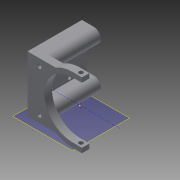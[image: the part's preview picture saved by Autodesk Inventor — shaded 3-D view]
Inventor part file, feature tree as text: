
AUTODESK INVENTOR PART (.ipt)
format: ipt  version: 2015 SP2 (Build 190223200, 223)  size: 181,248 bytes
history: native  units: mm
features: sketch x8, extrude x4, hole x3, plane x1
ambient origin geometry x8: Origin, YZ Plane, XZ Plane, XY Plane, X Axis, Y Axis, Z Axis, Center Point
bodies: Solid1 (feature_tree)
feature tree (16):
  extrude  "Extrusion1"  Depth=50.0mm TaperAngle=0.0deg
  extrude  "Extrusion2"  Depth=10.0mm
  extrude  "Extrusion3"  Depth=15.0mm
  hole  "Hole1"  [1 undecoded]
  plane  "Work Plane1"
  hole  "Hole2"  [1 undecoded]
  sketch  "Sketch7"  dims[d36=4.5mm d37=6.0mm d38=10.59mm d39=3.0mm d40=90.0deg d41=8.0mm d42=20.594885mm d44=4.0mm d45=0.0mm]
  hole  "Hole3"  [1 undecoded]
  extrude  "Extrusion4"  [1 undecoded]
  sketch  "Sketch1"  dims[d5=0.0mm d7=50.0mm d8=0.0mm]
  sketch  "Sketch2"  dims[d12=50.0mm d13=0.0mm]
  sketch  "Sketch3"  dims[d17=3.4mm d18=6.0mm d19=4.0mm d20=2.0mm d21=90.0deg d22=8.0mm d23=20.594885mm]
  sketch  "Sketch4"  dims[d26=4.5mm d27=6.0mm d28=4.0mm d29=2.0mm d30=90.0deg d31=8.0mm d32=20.594885mm d33=10.0mm]
  sketch  "Sketch5"  dims[d34=5.0mm d35=15.0mm]
  sketch  "Sketch8"
  sketch  "Sketch9"
note: 4 required parameter values undecoded (feature->parameter linkage not recoverable at this tier; creation-order binding heuristic only, values carry confidence <= 0.55)
